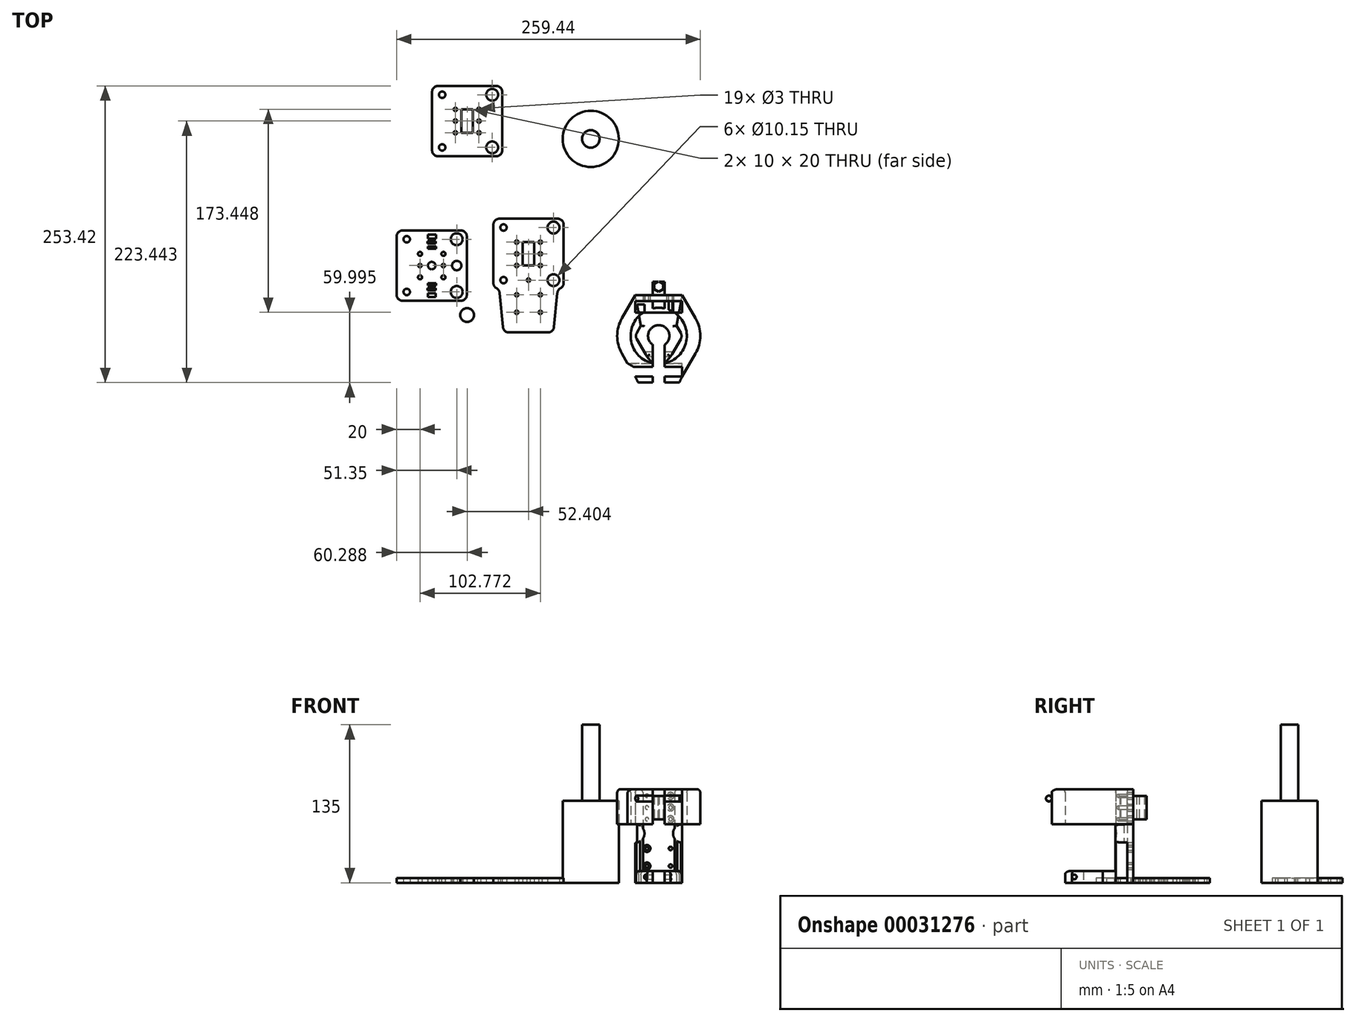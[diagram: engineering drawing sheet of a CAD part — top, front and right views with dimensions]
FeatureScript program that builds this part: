
annotation { "Feature Type Name" : "Feature", "Feature Type Description" : "" }
export const myFeature = defineFeature(function(context is Context, id is Id, definition is map)
    precondition{}
    {
        {
            var Q0;
            Q0=qCreatedBy(makeId("Top.planeOp"),FACE);
            var sketch = newSketch(context, id + "F0", { "sketchPlane" : qUnion([Q0])});
            skArc(sketch, "E0", {"start": v(24.79, -19.87) * mm, "mid": v(28.33, -18.4) * mm, "end": v(29.79, -14.87) * mm});
            skLineSegment(sketch, "E1", {"start": v(24.79, -19.87) * mm, "end": v(-25.21, -19.87) * mm});
            skArc(sketch, "E2", {"start": v(29.79, 35.13) * mm, "mid": v(28.33, 38.67) * mm, "end": v(24.79, 40.13) * mm});
            skLineSegment(sketch, "E3", {"start": v(29.79, 35.13) * mm, "end": v(29.79, -14.87) * mm});
            skArc(sketch, "E4", {"start": v(-25.21, 40.13) * mm, "mid": v(-28.75, 38.67) * mm, "end": v(-30.21, 35.13) * mm});
            skLineSegment(sketch, "E5", {"start": v(-25.21, 40.13) * mm, "end": v(24.79, 40.13) * mm});
            skArc(sketch, "E6", {"start": v(-30.21, -14.87) * mm, "mid": v(-28.75, -18.4) * mm, "end": v(-25.21, -19.87) * mm});
            skLineSegment(sketch, "E7", {"start": v(-30.21, -14.87) * mm, "end": v(-30.21, 35.13) * mm});
            skCircle(sketch, "E8", {"center": v(30, -32.16) * mm, "radius": 5.9 * mm});
            skCircle(sketch, "E9", {"center": v(-30, -32.16) * mm, "radius": 5.9 * mm});
            skLineSegment(sketch, "E10", {"start": v(-30.85, -40.13) * mm, "end": v(30.85, -40.13) * mm});
            skArc(sketch, "E11", {"start": v(30.85, -40.13) * mm, "mid": v(36.61, -37.74) * mm, "end": v(39, -31.98) * mm});
            skArc(sketch, "E12", {"start": v(39, -31.98) * mm, "mid": v(36.61, -26.22) * mm, "end": v(30.85, -23.83) * mm});
            skLineSegment(sketch, "E13", {"start": v(30.85, -23.83) * mm, "end": v(-30.85, -23.83) * mm});
            skArc(sketch, "E14", {"start": v(-30.85, -23.83) * mm, "mid": v(-36.61, -26.22) * mm, "end": v(-39, -31.98) * mm});
            skArc(sketch, "E15", {"start": v(-39, -31.98) * mm, "mid": v(-36.61, -37.74) * mm, "end": v(-30.85, -40.13) * mm});
            skCircle(sketch, "E16", {"center": v(21.14, 32.63) * mm, "radius": 5.08 * mm});
            skCircle(sketch, "E17", {"center": v(21.14, -12.37) * mm, "radius": 5.08 * mm});
            skCircle(sketch, "E18", {"center": v(-21.56, 32.63) * mm, "radius": 2.75 * mm});
            skCircle(sketch, "E19", {"center": v(-21.56, -12.37) * mm, "radius": 2.75 * mm});
            skCircle(sketch, "E20", {"center": v(-10.21, 20.13) * mm, "radius": 1.75 * mm});
            skCircle(sketch, "E21", {"center": v(-10.21, 0.13) * mm, "radius": 1.75 * mm});
            skCircle(sketch, "E22", {"center": v(9.79, 0.13) * mm, "radius": 1.75 * mm});
            skCircle(sketch, "E23", {"center": v(9.79, 20.13) * mm, "radius": 1.75 * mm});
            skLineSegment(sketch, "E24", {"start": v(-3.63, -6.88) * mm, "end": v(3.37, -6.88) * mm});
            skLineSegment(sketch, "E25", {"start": v(3.37, -6.88) * mm, "end": v(3.37, -4.88) * mm});
            skLineSegment(sketch, "E26", {"start": v(3.37, -4.88) * mm, "end": v(-3.63, -4.88) * mm});
            skLineSegment(sketch, "E27", {"start": v(-3.63, -4.88) * mm, "end": v(-3.63, -6.88) * mm});
            skLineSegment(sketch, "E28", {"start": v(-3.66, -11.08) * mm, "end": v(3.34, -11.08) * mm});
            skLineSegment(sketch, "E29", {"start": v(3.34, -11.08) * mm, "end": v(3.34, -9.08) * mm});
            skLineSegment(sketch, "E30", {"start": v(3.34, -9.08) * mm, "end": v(-3.66, -9.08) * mm});
            skLineSegment(sketch, "E31", {"start": v(-3.66, -9.08) * mm, "end": v(-3.66, -11.08) * mm});
            skLineSegment(sketch, "E32", {"start": v(3.35, -16.82) * mm, "end": v(3.35, -13.38) * mm});
            skLineSegment(sketch, "E33", {"start": v(3.35, -13.38) * mm, "end": v(-3.63, -13.38) * mm});
            skLineSegment(sketch, "E34", {"start": v(-3.63, 33.12) * mm, "end": v(3.37, 33.12) * mm});
            skLineSegment(sketch, "E35", {"start": v(3.37, 33.12) * mm, "end": v(3.37, 36.53) * mm});
            skLineSegment(sketch, "E36", {"start": v(3.37, 36.53) * mm, "end": v(-3.63, 36.52) * mm});
            skLineSegment(sketch, "E37", {"start": v(-3.63, 36.52) * mm, "end": v(-3.63, 33.12) * mm});
            skLineSegment(sketch, "E38", {"start": v(-3.66, 28.92) * mm, "end": v(3.34, 28.92) * mm});
            skLineSegment(sketch, "E39", {"start": v(3.34, 28.92) * mm, "end": v(3.34, 30.92) * mm});
            skLineSegment(sketch, "E40", {"start": v(3.34, 30.92) * mm, "end": v(-3.66, 30.92) * mm});
            skLineSegment(sketch, "E41", {"start": v(-3.66, 30.92) * mm, "end": v(-3.66, 28.92) * mm});
            skLineSegment(sketch, "E42", {"start": v(-3.63, 24.62) * mm, "end": v(3.37, 24.62) * mm});
            skLineSegment(sketch, "E43", {"start": v(3.37, 24.62) * mm, "end": v(3.37, 26.62) * mm});
            skLineSegment(sketch, "E44", {"start": v(3.37, 26.62) * mm, "end": v(-3.63, 26.62) * mm});
            skLineSegment(sketch, "E45", {"start": v(-3.63, 26.62) * mm, "end": v(-3.63, 24.62) * mm});
            skCircle(sketch, "E46", {"center": v(-10.21, 10.13) * mm, "radius": 1.5 * mm});
            skCircle(sketch, "E47", {"center": v(9.79, 10.13) * mm, "radius": 1.5 * mm});
            skCircle(sketch, "E48", {"center": v(-10.18, -31.98) * mm, "radius": 1.5 * mm});
            skCircle(sketch, "E49", {"center": v(9.82, -31.98) * mm, "radius": 1.5 * mm});
            skCircle(sketch, "E50", {"center": v(-0.21, 10.13) * mm, "radius": 3.2 * mm});
            skPoint(sketch, "E51", {"position": v(-3.63, 36.52) * mm});
            skLineSegment(sketch, "E52", {"start": v(-3.63, -16.82) * mm, "end": v(3.35, -16.82) * mm});
            skLineSegment(sketch, "E53", {"start": v(-3.63, -16.82) * mm, "end": v(-3.63, -13.38) * mm});
            skCircle(sketch, "E54", {"center": v(21.14, 10.13) * mm, "radius": 4 * mm});
            skLineSegment(sketch, "E55", {"start": v(112.48, 45.2) * mm, "end": v(112.48, -4.8) * mm});
            skLineSegment(sketch, "E56", {"start": v(57.48, 50.2) * mm, "end": v(107.48, 50.2) * mm});
            skLineSegment(sketch, "E57", {"start": v(52.48, -4.8) * mm, "end": v(52.48, 45.2) * mm});
            skCircle(sketch, "E58", {"center": v(103.83, 42.7) * mm, "radius": 5.08 * mm});
            skCircle(sketch, "E59", {"center": v(103.83, -2.3) * mm, "radius": 5.08 * mm});
            skCircle(sketch, "E60", {"center": v(61.13, -2.3) * mm, "radius": 2.75 * mm});
            skCircle(sketch, "E61", {"center": v(61.13, 42.7) * mm, "radius": 2.75 * mm});
            skArc(sketch, "E62", {"start": v(109.8, -9.23) * mm, "mid": v(111.76, -7.4) * mm, "end": v(112.48, -4.8) * mm});
            skArc(sketch, "E63", {"start": v(112.48, 45.2) * mm, "mid": v(111.02, 48.73) * mm, "end": v(107.48, 50.2) * mm});
            skArc(sketch, "E64", {"start": v(57.48, 50.2) * mm, "mid": v(53.95, 48.73) * mm, "end": v(52.48, 45.2) * mm});
            skArc(sketch, "E65", {"start": v(52.48, -4.8) * mm, "mid": v(53.95, -8.34) * mm, "end": v(57.48, -9.8) * mm});
            skLineSegment(sketch, "E66", {"start": v(82.48, -47) * mm, "end": v(82.48, -9.8) * mm, "construction": true});
            skLineSegment(sketch, "E67", {"start": v(82.48, -47) * mm, "end": v(99.3, -47) * mm});
            skLineSegment(sketch, "E68", {"start": v(107.15, -13.17) * mm, "end": v(104.27, -42.49) * mm});
            skPoint(sketch, "E69.visualSharp", {"position": v(107.48, -9.8) * mm});
            skArc(sketch, "E69.filletArc", {"start": v(109.8, -9.23) * mm, "mid": v(107.98, -10.87) * mm, "end": v(107.15, -13.17) * mm});
            skPoint(sketch, "E70.visualSharp", {"position": v(103.83, -47) * mm});
            skArc(sketch, "E70.filletArc", {"start": v(99.3, -47) * mm, "mid": v(102.66, -45.7) * mm, "end": v(104.27, -42.49) * mm});
            skLineSegment(sketch, "E71.MirrorCS", {"start": v(82.48, -47) * mm, "end": v(65.66, -47) * mm});
            skArc(sketch, "E72.MirrorCS", {"start": v(65.66, -47) * mm, "mid": v(62.3, -45.7) * mm, "end": v(60.69, -42.49) * mm});
            skLineSegment(sketch, "E73.MirrorCS", {"start": v(57.81, -13.17) * mm, "end": v(60.69, -42.49) * mm});
            skArc(sketch, "E74.MirrorCS", {"start": v(55.16, -9.23) * mm, "mid": v(56.98, -10.87) * mm, "end": v(57.81, -13.17) * mm});
            skLineSegment(sketch, "E75", {"start": v(82.48, 30.21) * mm, "end": v(87.48, 30.21) * mm});
            skLineSegment(sketch, "E76.bottom", {"start": v(87.48, 30.21) * mm, "end": v(77.48, 30.21) * mm});
            skLineSegment(sketch, "E76.left", {"start": v(87.48, 30.21) * mm, "end": v(87.48, 10.21) * mm});
            skLineSegment(sketch, "E76.right", {"start": v(77.48, 30.21) * mm, "end": v(77.48, 10.21) * mm});
            skLineSegment(sketch, "E77", {"start": v(92.56, 30.21) * mm, "end": v(92.56, 10.21) * mm, "construction": true});
            skLineSegment(sketch, "E78", {"start": v(87.48, 10.21) * mm, "end": v(77.48, 10.21) * mm});
            skCircle(sketch, "E79", {"center": v(92.56, 30.21) * mm, "radius": 1.5 * mm});
            skCircle(sketch, "E80", {"center": v(92.56, 20.21) * mm, "radius": 1.5 * mm});
            skCircle(sketch, "E81", {"center": v(92.56, 10.21) * mm, "radius": 1.5 * mm});
            skLineSegment(sketch, "E82", {"start": v(92.56, 10.21) * mm, "end": v(92.56, -14.79) * mm, "construction": true});
            skLineSegment(sketch, "E83", {"start": v(92.56, -14.79) * mm, "end": v(92.56, -29.79) * mm, "construction": true});
            skCircle(sketch, "E84", {"center": v(92.56, -14.79) * mm, "radius": 1.5 * mm});
            skCircle(sketch, "E85", {"center": v(92.56, -29.79) * mm, "radius": 1.5 * mm});
            skCircle(sketch, "E86.MirrorC", {"center": v(72.4, -14.79) * mm, "radius": 1.5 * mm});
            skCircle(sketch, "E87.MirrorC", {"center": v(72.4, -29.79) * mm, "radius": 1.5 * mm});
            skCircle(sketch, "E88.MirrorC", {"center": v(72.4, 10.21) * mm, "radius": 1.5 * mm});
            skCircle(sketch, "E89.MirrorC", {"center": v(72.4, 20.21) * mm, "radius": 1.5 * mm});
            skCircle(sketch, "E90.MirrorC", {"center": v(72.4, 30.21) * mm, "radius": 1.5 * mm});
            skLineSegment(sketch, "E91", {"start": v(60.08, 158.64) * mm, "end": v(60.08, 108.64) * mm});
            skLineSegment(sketch, "E92", {"start": v(5.08, 163.64) * mm, "end": v(55.08, 163.64) * mm});
            skLineSegment(sketch, "E93", {"start": v(0.08, 108.64) * mm, "end": v(0.08, 158.64) * mm});
            skCircle(sketch, "E94", {"center": v(51.43, 156.14) * mm, "radius": 5.08 * mm});
            skPoint(sketch, "E95.visualSharp", {"position": v(55.08, 103.64) * mm});
            skLineSegment(sketch, "E96.right", {"start": v(25.08, 143.66) * mm, "end": v(25.08, 123.66) * mm});
            skLineSegment(sketch, "E96.left", {"start": v(35.08, 143.66) * mm, "end": v(35.08, 123.66) * mm});
            skLineSegment(sketch, "E97", {"start": v(40.16, 143.66) * mm, "end": v(40.16, 123.66) * mm, "construction": true});
            skCircle(sketch, "E98", {"center": v(51.43, 111.14) * mm, "radius": 5.08 * mm});
            skCircle(sketch, "E99.MirrorC", {"center": v(20, 133.66) * mm, "radius": 1.5 * mm});
            skCircle(sketch, "E100", {"center": v(8.73, 111.14) * mm, "radius": 2.75 * mm});
            skCircle(sketch, "E101.MirrorC", {"center": v(20, 143.66) * mm, "radius": 1.5 * mm});
            skCircle(sketch, "E102", {"center": v(8.73, 156.14) * mm, "radius": 2.75 * mm});
            skCircle(sketch, "E103", {"center": v(40.16, 133.66) * mm, "radius": 1.5 * mm});
            skCircle(sketch, "E104.MirrorC", {"center": v(20, 123.66) * mm, "radius": 1.5 * mm});
            skLineSegment(sketch, "E96.bottom", {"start": v(35.08, 143.66) * mm, "end": v(25.08, 143.66) * mm});
            skArc(sketch, "E105", {"start": v(60.08, 158.64) * mm, "mid": v(58.61, 162.18) * mm, "end": v(55.08, 163.64) * mm});
            skLineSegment(sketch, "E106", {"start": v(35.08, 123.66) * mm, "end": v(25.08, 123.66) * mm});
            skArc(sketch, "E107", {"start": v(5.08, 163.64) * mm, "mid": v(1.54, 162.18) * mm, "end": v(0.08, 158.64) * mm});
            skCircle(sketch, "E108", {"center": v(40.16, 143.66) * mm, "radius": 1.5 * mm});
            skArc(sketch, "E109", {"start": v(0.08, 108.64) * mm, "mid": v(1.54, 105.1) * mm, "end": v(5.08, 103.64) * mm});
            skLineSegment(sketch, "E110", {"start": v(30.08, 143.66) * mm, "end": v(35.08, 143.66) * mm});
            skLineSegment(sketch, "E111", {"start": v(5.08, 103.64) * mm, "end": v(55.08, 103.64) * mm});
            skLineSegment(sketch, "E112", {"start": v(60.08, 108.64) * mm, "end": v(60.08, 108.64) * mm});
            skPoint(sketch, "E113.visualSharp", {"position": v(60.08, 103.64) * mm});
            skArc(sketch, "E113.filletArc", {"start": v(55.08, 103.64) * mm, "mid": v(58.61, 105.1) * mm, "end": v(60.08, 108.64) * mm});
            skCircle(sketch, "E114.MirrorC", {"center": v(40.16, 123.66) * mm, "radius": 1.5 * mm});
            skCircle(sketch, "E115", {"center": v(135.68, 118.4) * mm, "radius": 24 * mm});
            skCircle(sketch, "E116", {"center": v(135.68, 118.4) * mm, "radius": 7.5 * mm});
            skLineSegment(sketch, "E117", {"start": v(61.13, -2.3) * mm, "end": v(103.83, -2.3) * mm, "construction": true});
            skCircle(sketch, "E118", {"center": v(82.48, -2.3) * mm, "radius": 1.5 * mm});
            skArc(sketch, "E119.MirrorCS", {"start": v(112.48, -4.8) * mm, "mid": v(111.02, -8.34) * mm, "end": v(107.48, -9.8) * mm});
            skLineSegment(sketch, "E120", {"start": v(57.48, -9.8) * mm, "end": v(107.48, -9.8) * mm, "construction": true});
            skSolve(sketch);
        }
        {
            var Q0;
            Q0=makeQuery(id+"F0.imprint","IMPRINT",FACE,{"disambiguationData":[TD([[makeQuery(id+"F0.imprint","IMPRINT",EDGE,{"derivedFrom":sQuery(id+"F0.wireOp",EDGE,"E0")}),1.0]])]});
            var Q1;
            Q1=makeQuery(id+"F0.imprint","IMPRINT",FACE,{"disambiguationData":[TD([[makeQuery(id+"F0.imprint","IMPRINT",EDGE,{"derivedFrom":sQuery(id+"F0.wireOp",EDGE,"E8")}),1.0]])]});
            var Q2;
            Q2=makeQuery(id+"F0.imprint","IMPRINT",FACE,{"disambiguationData":[TD([[makeQuery(id+"F0.imprint","IMPRINT",EDGE,{"derivedFrom":sQuery(id+"F0.wireOp",EDGE,"f96d0108-ce3c-40f9-9041-a5f02a56c2c8")}),-1.0]])]});
            var Q3;
            Q3=makeQuery(id+"F0.imprint","IMPRINT",FACE,{"disambiguationData":[TD([[makeQuery(id+"F0.imprint","IMPRINT",EDGE,{"derivedFrom":sQuery(id+"F0.wireOp",EDGE,"fc6a74a1-8ae2-464b-8a54-e97a179053b1")}),1.0]])]});
            var Q4;
            Q4=makeQuery(id+"F0.imprint","IMPRINT",FACE,{"disambiguationData":[TD([[makeQuery(id+"F0.imprint","IMPRINT",EDGE,{"derivedFrom":sQuery(id+"F0.wireOp",EDGE,"E55")}),-1.0]])]});
            var Q5;
            Q5=makeQuery(id+"F0.imprint","IMPRINT",FACE,{"disambiguationData":[TD([[makeQuery(id+"F0.imprint","IMPRINT",EDGE,{"derivedFrom":sQuery(id+"F0.wireOp",EDGE,"E91")}),-1.0]])]});
            extrude(context, id + "F1", {"entities" : qUnion([Q0, Q1, Q2, Q3, Q4, Q5]), "depth" : 4 * mm});
        }
        {
            var Q0;
            Q0=qCreatedBy(makeId("Top.planeOp"),FACE);
            var sketch = newSketch(context, id + "F2", { "sketchPlane" : qUnion([Q0])});
            skCircle(sketch, "E121", {"center": v(193.74, -49.93) * mm, "radius": 9.15 * mm});
            skCircle(sketch, "E122.cCircle", {"center": v(193.74, -49.93) * mm, "radius": 17.57 * mm, "construction": true});
            skLineSegment(sketch, "E122.0", {"start": v(183.6, -32.36) * mm, "end": v(203.89, -32.36) * mm});
            skLineSegment(sketch, "E122.1", {"start": v(203.89, -32.36) * mm, "end": v(212.59, -47.43) * mm});
            skLineSegment(sketch, "E122.2", {"start": v(212.59, -52.43) * mm, "end": v(203.89, -67.5) * mm});
            skLineSegment(sketch, "E122.3", {"start": v(203.89, -67.5) * mm, "end": v(183.6, -67.5) * mm});
            skLineSegment(sketch, "E122.4", {"start": v(183.6, -67.5) * mm, "end": v(174.9, -52.43) * mm});
            skLineSegment(sketch, "E122.5", {"start": v(174.9, -47.43) * mm, "end": v(183.6, -32.36) * mm});
            skPoint(sketch, "E122.0.midPoint", {"position": v(193.74, -32.36) * mm});
            skCircle(sketch, "E123", {"center": v(193.74, -49.93) * mm, "radius": 24 * mm});
            skCircle(sketch, "E124.cCircle", {"center": v(193.74, -49.93) * mm, "radius": 34.75 * mm, "construction": true});
            skLineSegment(sketch, "E124.0", {"start": v(173.68, -15.18) * mm, "end": v(213.8, -15.18) * mm});
            skLineSegment(sketch, "E124.1", {"start": v(213.8, -15.18) * mm, "end": v(225.21, -34.93) * mm});
            skLineSegment(sketch, "E124.2", {"start": v(225.21, -64.93) * mm, "end": v(213.8, -84.68) * mm});
            skLineSegment(sketch, "E124.3", {"start": v(213.8, -84.68) * mm, "end": v(173.68, -84.68) * mm});
            skLineSegment(sketch, "E124.4", {"start": v(173.68, -84.68) * mm, "end": v(162.28, -64.93) * mm});
            skLineSegment(sketch, "E124.5", {"start": v(162.28, -34.93) * mm, "end": v(173.68, -15.18) * mm});
            skPoint(sketch, "E124.0.midPoint", {"position": v(193.74, -15.18) * mm});
            skLineSegment(sketch, "E125", {"start": v(193.74, -49.93) * mm, "end": v(193.74, -99) * mm, "construction": true});
            skPoint(sketch, "E125.endSnap0", {"position": v(193.74, -84.68) * mm});
            skLineSegment(sketch, "E126", {"start": v(193.74, -99) * mm, "end": v(198.74, -99) * mm, "construction": true});
            skLineSegment(sketch, "E127", {"start": v(198.74, -99) * mm, "end": v(198.74, -57.6) * mm});
            skLineSegment(sketch, "E128", {"start": v(198.74, -99) * mm, "end": v(206.95, -99) * mm});
            skLineSegment(sketch, "E129", {"start": v(206.95, -99) * mm, "end": v(213.8, -84.68) * mm});
            skLineSegment(sketch, "E130.MirrorCS", {"start": v(188.74, -99) * mm, "end": v(188.74, -57.6) * mm});
            skLineSegment(sketch, "E131.MirrorCS", {"start": v(188.74, -99) * mm, "end": v(180.54, -99) * mm});
            skLineSegment(sketch, "E132.MirrorCS", {"start": v(180.54, -99) * mm, "end": v(173.68, -84.68) * mm});
            skLineSegment(sketch, "E133", {"start": v(183.6, -67.5) * mm, "end": v(188.74, -73.4) * mm});
            skLineSegment(sketch, "E134.MirrorCS", {"start": v(203.89, -67.5) * mm, "end": v(198.74, -73.4) * mm, "construction": true});
            skLineSegment(sketch, "E135.MirrorCS", {"start": v(203.89, -67.5) * mm, "end": v(198.74, -73.4) * mm});
            skLineSegment(sketch, "E136", {"start": v(193.74, -49.93) * mm, "end": v(203.74, -49.93) * mm, "construction": true});
            skLineSegment(sketch, "E137", {"start": v(203.74, -49.93) * mm, "end": v(203.74, -15.18) * mm, "construction": true});
            skLineSegment(sketch, "E138.MirrorCS", {"start": v(183.74, -49.93) * mm, "end": v(183.74, -15.18) * mm, "construction": true});
            skLineSegment(sketch, "E139", {"start": v(178.53, -41.15) * mm, "end": v(173.68, -15.18) * mm});
            skLineSegment(sketch, "E140", {"start": v(208.96, -41.15) * mm, "end": v(213.8, -15.18) * mm});
            skPoint(sketch, "E141.visualSharp", {"position": v(153.62, -49.93) * mm});
            skArc(sketch, "E141.filletArc", {"start": v(162.28, -34.93) * mm, "mid": v(158.26, -49.93) * mm, "end": v(162.28, -64.93) * mm});
            skPoint(sketch, "E142.visualSharp", {"position": v(233.87, -49.93) * mm});
            skArc(sketch, "E142.filletArc", {"start": v(225.21, -64.93) * mm, "mid": v(229.23, -49.93) * mm, "end": v(225.21, -34.93) * mm});
            skPoint(sketch, "E143.visualSharp", {"position": v(173.46, -49.93) * mm});
            skArc(sketch, "E143.filletArc", {"start": v(174.9, -47.43) * mm, "mid": v(174.23, -49.93) * mm, "end": v(174.9, -52.43) * mm});
            skPoint(sketch, "E144.visualSharp", {"position": v(214.03, -49.93) * mm});
            skArc(sketch, "E144.filletArc", {"start": v(212.59, -52.43) * mm, "mid": v(213.26, -49.93) * mm, "end": v(212.59, -47.43) * mm});
            skCircle(sketch, "E145.cCircle", {"center": v(193.74, -7.9) * mm, "radius": 4.4 * mm, "construction": true});
            skLineSegment(sketch, "E145.0", {"start": v(193.74, -3.5) * mm, "end": v(197.55, -5.7) * mm});
            skLineSegment(sketch, "E145.1", {"start": v(197.55, -5.7) * mm, "end": v(197.55, -10.1) * mm});
            skLineSegment(sketch, "E145.2", {"start": v(197.55, -10.1) * mm, "end": v(193.74, -12.3) * mm});
            skLineSegment(sketch, "E145.3", {"start": v(193.74, -12.3) * mm, "end": v(189.94, -10.1) * mm});
            skLineSegment(sketch, "E145.4", {"start": v(189.94, -10.1) * mm, "end": v(189.94, -5.7) * mm});
            skLineSegment(sketch, "E145.5", {"start": v(189.94, -5.7) * mm, "end": v(193.74, -3.5) * mm});
            skCircle(sketch, "E146", {"center": v(193.74, -7.9) * mm, "radius": 2.5 * mm});
            skLineSegment(sketch, "E147", {"start": v(193.74, -15.18) * mm, "end": v(193.74, -11.18) * mm, "construction": true});
            skLineSegment(sketch, "E148", {"start": v(193.74, -11.18) * mm, "end": v(193.74, -7.9) * mm, "construction": true});
            skSolve(sketch);
        }
        {
            var Q0;
            {var subQ0=sQuery(id+"F2.wireOp",EDGE,"96ee02a5-edc4-4475-906e-b3a8b5a1a6cf");var subQ1=sQuery(id+"F2.wireOp",EDGE,"E123");var subQ2=makeQuery(id+"F2.imprint","INTERSECT",VERTEX,{"derivedFrom":[subQ1,subQ0]});Q0=makeQuery(id+"F2.imprint","IMPRINT",FACE,{"disambiguationData":[TD([[makeQuery(id+"F2.imprint","IMPRINT",EDGE,{"disambiguationData":[TD([[subQ2,1.0]])],"derivedFrom":subQ1}),-1.0]])]});}
            var Q1;
            {var subQ5=sQuery(id+"F2.wireOp",EDGE,"E124.0");Q1=makeQuery(id+"F2.imprint","IMPRINT",FACE,{"disambiguationData":[TD([[makeQuery(id+"F2.imprint","IMPRINT",EDGE,{"derivedFrom":subQ5}),-1.0]])]});}
            var Q2;
            {var subQ11=sQuery(id+"F2.wireOp",EDGE,"E122.0");Q2=makeQuery(id+"F2.imprint","IMPRINT",FACE,{"disambiguationData":[TD([[makeQuery(id+"F2.imprint","IMPRINT",EDGE,{"derivedFrom":subQ11}),-1.0]])]});}
            var Q3;
            {var subQ8=sQuery(id+"F2.wireOp",EDGE,"E122.0");Q3=makeQuery(id+"F2.imprint","IMPRINT",FACE,{"disambiguationData":[TD([[makeQuery(id+"F2.imprint","IMPRINT",EDGE,{"derivedFrom":subQ8}),1.0]])]});}
            var Q4;
            {var subQ0=sQuery(id+"F2.wireOp",EDGE,"E135.MirrorCS");Q4=makeQuery(id+"F2.imprint","IMPRINT",FACE,{"disambiguationData":[TD([[makeQuery(id+"F2.imprint","IMPRINT",EDGE,{"derivedFrom":subQ0}),-1.0]])]});}
            var Q5;
            {var subQ0=sQuery(id+"F2.wireOp",EDGE,"E133");Q5=makeQuery(id+"F2.imprint","IMPRINT",FACE,{"disambiguationData":[TD([[makeQuery(id+"F2.imprint","IMPRINT",EDGE,{"derivedFrom":subQ0}),1.0]])]});}
            extrude(context, id + "F3", {"entities" : qUnion([Q0, Q1, Q2, Q3, Q4, Q5]), "depth" : 10 * mm});
        }
        {
            var Q0;
            {var subQ5=sQuery(id+"F2.wireOp",EDGE,"E124.0");Q0=makeQuery(id+"F2.imprint","IMPRINT",FACE,{"disambiguationData":[TD([[makeQuery(id+"F2.imprint","IMPRINT",EDGE,{"derivedFrom":subQ5}),-1.0]])]});}
            extrude(context, id + "F4", {"entities" : qUnion([Q0]), "operationType" : NewBodyOperationType.ADD, "depth" : 80 * mm, "hasSecondDirection" : true, "secondDirectionOppositeDirection" : false, "secondDirectionDepth" : 10 * mm});
        }
        {
            var Q0;
            {var subQ1=sQuery(id+"F2.wireOp",EDGE,"E124.4");Q0=makeQuery(id+"F2.imprint","IMPRINT",FACE,{"disambiguationData":[TD([[makeQuery(id+"F2.imprint","IMPRINT",EDGE,{"derivedFrom":subQ1}),-1.0]])]});}
            var Q1;
            {var subQ4=sQuery(id+"F2.wireOp",EDGE,"E131.MirrorCS");Q1=makeQuery(id+"F2.imprint","IMPRINT",FACE,{"disambiguationData":[TD([[makeQuery(id+"F2.imprint","IMPRINT",EDGE,{"derivedFrom":subQ4}),-1.0]])]});}
            var Q2;
            {var subQ4=sQuery(id+"F2.wireOp",EDGE,"E128");Q2=makeQuery(id+"F2.imprint","IMPRINT",FACE,{"disambiguationData":[TD([[makeQuery(id+"F2.imprint","IMPRINT",EDGE,{"derivedFrom":subQ4}),1.0]])]});}
            var Q3;
            {var subQ6=sQuery(id+"F2.wireOp",EDGE,"E124.1");Q3=makeQuery(id+"F2.imprint","IMPRINT",FACE,{"disambiguationData":[TD([[makeQuery(id+"F2.imprint","IMPRINT",EDGE,{"derivedFrom":subQ6}),-1.0]])]});}
            var Q4;
            {var subQ5=sQuery(id+"F2.wireOp",EDGE,"E124.0");Q4=makeQuery(id+"F2.imprint","IMPRINT",FACE,{"disambiguationData":[TD([[makeQuery(id+"F2.imprint","IMPRINT",EDGE,{"derivedFrom":subQ5}),-1.0]])]});}
            extrude(context, id + "F5", {"entities" : qUnion([Q0, Q1, Q2, Q3, Q4]), "operationType" : NewBodyOperationType.ADD, "depth" : 80 * mm, "hasSecondDirection" : true, "secondDirectionOppositeDirection" : false, "secondDirectionDepth" : 50 * mm});
        }
        {
            var Q0;
            {var subQ0=sQuery(id+"F2.wireOp",EDGE,"E124.0");Q0=makeQuery(id+"F4.boolean.opBoolean","MERGE",FACE,{"derivedFrom":[makeQuery(id+"F3.opExtrude","SWEPT_FACE",FACE,{"disambiguationData":[OSD([subQ0])]}),makeQuery(id+"F4.opExtrude","SWEPT_FACE",FACE,{"disambiguationData":[OSD([subQ0])]})]});}
            var sketch = newSketch(context, id + "F6", { "sketchPlane" : qUnion([Q0])});
            skLineSegment(sketch, "E149", {"start": v(-193.74, 64.3) * mm, "end": v(-198.74, 64.3) * mm, "construction": true});
            skLineSegment(sketch, "E150", {"start": v(-198.74, 64.3) * mm, "end": v(-198.74, 54.3) * mm, "construction": true});
            skLineSegment(sketch, "E151", {"start": v(-198.74, 54.3) * mm, "end": v(-193.74, 54.3) * mm, "construction": true});
            skLineSegment(sketch, "E152.bottom", {"start": v(-198.74, 54.3) * mm, "end": v(-188.74, 54.3) * mm});
            skLineSegment(sketch, "E152.top", {"start": v(-198.74, 74.3) * mm, "end": v(-188.74, 74.3) * mm});
            skLineSegment(sketch, "E152.left", {"start": v(-198.74, 54.3) * mm, "end": v(-198.74, 74.3) * mm});
            skLineSegment(sketch, "E152.right", {"start": v(-188.74, 54.3) * mm, "end": v(-188.74, 74.3) * mm});
            skLineSegment(sketch, "E153", {"start": v(-188.74, 74.3) * mm, "end": v(-183.66, 74.3) * mm, "construction": true});
            skCircle(sketch, "E154", {"center": v(-183.66, 74.3) * mm, "radius": 1.5 * mm});
            skCircle(sketch, "E155", {"center": v(-183.66, 64.3) * mm, "radius": 1.5 * mm});
            skCircle(sketch, "E156", {"center": v(-183.66, 54.3) * mm, "radius": 1.5 * mm});
            skCircle(sketch, "E157", {"center": v(-173.68, 42.14) * mm, "radius": 7.86 * mm});
            skLineSegment(sketch, "E158", {"start": v(-193.74, 0) * mm, "end": v(-193.74, 29.82) * mm, "construction": true});
            skCircle(sketch, "E159.MirrorC", {"center": v(-213.8, 42.14) * mm, "radius": 7.86 * mm});
            skLineSegment(sketch, "E160", {"start": v(-193.74, 29.82) * mm, "end": v(-193.74, 54.3) * mm, "construction": true});
            skLineSegment(sketch, "E161", {"start": v(-203.82, 54.3) * mm, "end": v(-203.82, 29.3) * mm, "construction": true});
            skLineSegment(sketch, "E162", {"start": v(-203.82, 29.3) * mm, "end": v(-203.82, 14.3) * mm, "construction": true});
            skCircle(sketch, "E163", {"center": v(-203.82, 29.3) * mm, "radius": 1.5 * mm});
            skCircle(sketch, "E164", {"center": v(-203.82, 14.3) * mm, "radius": 1.5 * mm});
            skCircle(sketch, "E165.MirrorC", {"center": v(-183.66, 29.3) * mm, "radius": 1.5 * mm});
            skCircle(sketch, "E166.MirrorC", {"center": v(-183.66, 14.3) * mm, "radius": 1.5 * mm});
            skCircle(sketch, "E167", {"center": v(-183.66, 74.3) * mm, "radius": 3 * mm});
            skCircle(sketch, "E168", {"center": v(-183.66, 64.3) * mm, "radius": 3 * mm});
            skCircle(sketch, "E169", {"center": v(-183.66, 54.3) * mm, "radius": 3 * mm});
            skCircle(sketch, "E170", {"center": v(-183.66, 29.3) * mm, "radius": 3 * mm});
            skCircle(sketch, "E171", {"center": v(-183.66, 14.3) * mm, "radius": 3 * mm});
            skCircle(sketch, "E172.MirrorC", {"center": v(-203.82, 29.3) * mm, "radius": 3 * mm});
            skCircle(sketch, "E173.MirrorC", {"center": v(-203.82, 14.3) * mm, "radius": 3 * mm});
            skCircle(sketch, "E174.MirrorC", {"center": v(-203.82, 54.3) * mm, "radius": 3 * mm});
            skCircle(sketch, "E175.MirrorC", {"center": v(-203.82, 64.3) * mm, "radius": 3 * mm});
            skCircle(sketch, "E176.MirrorC", {"center": v(-203.82, 74.3) * mm, "radius": 3 * mm});
            skCircle(sketch, "E177.MirrorC", {"center": v(-203.82, 54.3) * mm, "radius": 1.5 * mm});
            skCircle(sketch, "E178.MirrorC", {"center": v(-203.82, 64.3) * mm, "radius": 1.5 * mm});
            skCircle(sketch, "E179.MirrorC", {"center": v(-203.82, 74.3) * mm, "radius": 1.5 * mm});
            skSolve(sketch);
        }
        {
            var Q0;
            Q0=makeQuery(id+"F6.imprint","IMPRINT",FACE,{"disambiguationData":[TD([[makeQuery(id+"F6.imprint","IMPRINT",EDGE,{"derivedFrom":sQuery(id+"F6.wireOp",EDGE,"E156")}),1.0]])]});
            var Q1;
            Q1=makeQuery(id+"F6.imprint","IMPRINT",FACE,{"disambiguationData":[TD([[makeQuery(id+"F6.imprint","IMPRINT",EDGE,{"derivedFrom":sQuery(id+"F6.wireOp",EDGE,"E155")}),1.0]])]});
            var Q2;
            Q2=makeQuery(id+"F6.imprint","IMPRINT",FACE,{"disambiguationData":[TD([[makeQuery(id+"F6.imprint","IMPRINT",EDGE,{"derivedFrom":sQuery(id+"F6.wireOp",EDGE,"E154")}),1.0]])]});
            var Q3;
            Q3=makeQuery(id+"F6.imprint","IMPRINT",FACE,{"disambiguationData":[TD([[makeQuery(id+"F6.imprint","IMPRINT",EDGE,{"derivedFrom":sQuery(id+"F6.wireOp",EDGE,"45766864-c449-461b-9b77-59a764d4195f0.MirrorC")}),-1.0]])]});
            var Q4;
            Q4=makeQuery(id+"F6.imprint","IMPRINT",FACE,{"disambiguationData":[TD([[makeQuery(id+"F6.imprint","IMPRINT",EDGE,{"derivedFrom":sQuery(id+"F6.wireOp",EDGE,"dd78de97-23d6-4229-883f-769f5d6694050.MirrorC")}),-1.0]])]});
            var Q5;
            Q5=makeQuery(id+"F6.imprint","IMPRINT",FACE,{"disambiguationData":[TD([[makeQuery(id+"F6.imprint","IMPRINT",EDGE,{"derivedFrom":sQuery(id+"F6.wireOp",EDGE,"2f0e754c-4723-4be7-9447-68277993e2870.MirrorC")}),-1.0]])]});
            var Q6;
            Q6=makeQuery(id+"F6.imprint","IMPRINT",FACE,{"disambiguationData":[TD([[makeQuery(id+"F6.imprint","IMPRINT",EDGE,{"derivedFrom":sQuery(id+"F6.wireOp",EDGE,"E177.MirrorC")}),-1.0]])]});
            var Q7;
            Q7=makeQuery(id+"F6.imprint","IMPRINT",FACE,{"disambiguationData":[TD([[makeQuery(id+"F6.imprint","IMPRINT",EDGE,{"derivedFrom":sQuery(id+"F6.wireOp",EDGE,"E178.MirrorC")}),-1.0]])]});
            var Q8;
            Q8=makeQuery(id+"F6.imprint","IMPRINT",FACE,{"disambiguationData":[TD([[makeQuery(id+"F6.imprint","IMPRINT",EDGE,{"derivedFrom":sQuery(id+"F6.wireOp",EDGE,"E179.MirrorC")}),-1.0]])]});
            var Q9;
            Q9=makeQuery(id+"F6.imprint","IMPRINT",FACE,{"disambiguationData":[TD([[makeQuery(id+"F6.imprint","IMPRINT",EDGE,{"derivedFrom":sQuery(id+"F6.wireOp",EDGE,"E163")}),1.0]])]});
            var Q10;
            Q10=makeQuery(id+"F6.imprint","IMPRINT",FACE,{"disambiguationData":[TD([[makeQuery(id+"F6.imprint","IMPRINT",EDGE,{"derivedFrom":sQuery(id+"F6.wireOp",EDGE,"E165.MirrorC")}),-1.0]])]});
            var Q11;
            Q11=makeQuery(id+"F6.imprint","IMPRINT",FACE,{"disambiguationData":[TD([[makeQuery(id+"F6.imprint","IMPRINT",EDGE,{"derivedFrom":sQuery(id+"F6.wireOp",EDGE,"E166.MirrorC")}),-1.0]])]});
            var Q12;
            Q12=makeQuery(id+"F6.imprint","IMPRINT",FACE,{"disambiguationData":[TD([[makeQuery(id+"F6.imprint","IMPRINT",EDGE,{"derivedFrom":sQuery(id+"F6.wireOp",EDGE,"E164")}),1.0]])]});
            extrude(context, id + "F7", {"entities" : qUnion([Q0, Q1, Q2, Q3, Q4, Q5, Q6, Q7, Q8, Q9, Q10, Q11, Q12]), "operationType" : NewBodyOperationType.REMOVE, "oppositeDirection" : true, "depth" : 25 * mm});
        }
        {
            var Q0;
            Q0=makeQuery(id+"F6.imprint","IMPRINT",FACE,{"disambiguationData":[TD([[makeQuery(id+"F6.imprint","IMPRINT",EDGE,{"derivedFrom":sQuery(id+"F6.wireOp",EDGE,"E152.bottom")}),1.0]])]});
            extrude(context, id + "F8", {"entities" : qUnion([Q0]), "operationType" : NewBodyOperationType.ADD, "depth" : 11.5 * mm});
        }
        {
            var Q0;
            {var subQ0=sQuery(id+"F6.wireOp",EDGE,"E159.MirrorC");var subQ1=sQuery(id+"F2.wireOp",EDGE,"E124.0");var subQ2=sQuery(id+"F2.wireOp",EDGE,"E140");var subQ3=sQuery(id+"F2.wireOp",EDGE,"E130.MirrorCS");var subQ4=sQuery(id+"F2.wireOp",EDGE,"E127");var subQ5=sQuery(id+"F2.wireOp",EDGE,"E124.1");var subQ6=makeQuery(id+"F4.boolean.opBoolean","MERGE",EDGE,{"derivedFrom":[makeQuery(id+"F3.opExtrude","SWEPT_EDGE",EDGE,{"disambiguationData":[OSD([subQ1,subQ5,subQ2])]}),makeQuery(id+"F4.opExtrude","SWEPT_EDGE",EDGE,{"disambiguationData":[OSD([subQ1,subQ5,subQ2])]})]});var subQ7=makeQuery(id+"F5.boolean.opBoolean","SPLIT",EDGE,{"disambiguationData":[TD([makeQuery(id+"F3.opExtrude","CAP_FACE",FACE,{"disambiguationData":[OSD([sQuery(id+"F2.wireOp",EDGE,"E121"),sQuery(id+"F2.wireOp",EDGE,"E122.1"),sQuery(id+"F2.wireOp",EDGE,"E122.2"),sQuery(id+"F2.wireOp",EDGE,"E122.4"),sQuery(id+"F2.wireOp",EDGE,"E122.5"),subQ1,subQ4,subQ3,sQuery(id+"F2.wireOp",EDGE,"E133"),sQuery(id+"F2.wireOp",EDGE,"E135.MirrorCS"),sQuery(id+"F2.wireOp",EDGE,"E139"),subQ2])],"isStart":true})])],"derivedFrom":subQ6});var subQ9=makeQuery(id+"F6.imprint","INTERSECT",VERTEX,{"derivedFrom":[subQ7,subQ0]});Q0=makeQuery(id+"F6.imprint","IMPRINT",FACE,{"disambiguationData":[TD([[makeQuery(id+"F6.imprint","IMPRINT",EDGE,{"disambiguationData":[TD([[subQ9,1.0]])],"derivedFrom":subQ0}),-1.0]])]});}
            var Q1;
            {var subQ0=sQuery(id+"F6.wireOp",EDGE,"E157");var subQ1=sQuery(id+"F2.wireOp",EDGE,"E124.0");var subQ2=sQuery(id+"F2.wireOp",EDGE,"E139");var subQ3=sQuery(id+"F2.wireOp",EDGE,"E130.MirrorCS");var subQ4=sQuery(id+"F2.wireOp",EDGE,"E127");var subQ5=sQuery(id+"F2.wireOp",EDGE,"E124.5");var subQ6=makeQuery(id+"F4.boolean.opBoolean","MERGE",EDGE,{"derivedFrom":[makeQuery(id+"F3.opExtrude","SWEPT_EDGE",EDGE,{"disambiguationData":[OSD([subQ1,subQ5,subQ2])]}),makeQuery(id+"F4.opExtrude","SWEPT_EDGE",EDGE,{"disambiguationData":[OSD([subQ1,subQ5,subQ2])]})]});var subQ7=makeQuery(id+"F5.boolean.opBoolean","SPLIT",EDGE,{"disambiguationData":[TD([makeQuery(id+"F3.opExtrude","CAP_FACE",FACE,{"disambiguationData":[OSD([sQuery(id+"F2.wireOp",EDGE,"E121"),sQuery(id+"F2.wireOp",EDGE,"E122.1"),sQuery(id+"F2.wireOp",EDGE,"E122.2"),sQuery(id+"F2.wireOp",EDGE,"E122.4"),sQuery(id+"F2.wireOp",EDGE,"E122.5"),subQ1,subQ4,subQ3,sQuery(id+"F2.wireOp",EDGE,"E133"),sQuery(id+"F2.wireOp",EDGE,"E135.MirrorCS"),subQ2,sQuery(id+"F2.wireOp",EDGE,"E140")])],"isStart":true})])],"derivedFrom":subQ6});var subQ9=makeQuery(id+"F6.imprint","INTERSECT",VERTEX,{"derivedFrom":[subQ7,subQ0]});Q1=makeQuery(id+"F6.imprint","IMPRINT",FACE,{"disambiguationData":[TD([[makeQuery(id+"F6.imprint","IMPRINT",EDGE,{"disambiguationData":[TD([[subQ9,1.0]])],"derivedFrom":subQ0}),1.0]])]});}
            extrude(context, id + "F9", {"entities" : qUnion([Q0, Q1]), "operationType" : NewBodyOperationType.REMOVE, "oppositeDirection" : true, "depth" : 8 * mm});
        }
        {
            var Q0;
            Q0=makeQuery(id+"F2.imprint","IMPRINT",FACE,{"disambiguationData":[TD([[makeQuery(id+"F2.imprint","IMPRINT",EDGE,{"derivedFrom":sQuery(id+"F2.wireOp",EDGE,"E146")}),1.0]])]});
            var Q1;
            Q1=makeQuery(id+"F2.imprint","IMPRINT",FACE,{"disambiguationData":[TD([[makeQuery(id+"F2.imprint","IMPRINT",EDGE,{"derivedFrom":sQuery(id+"F2.wireOp",EDGE,"E145.0")}),-1.0]])]});
            extrude(context, id + "F10", {"entities" : qUnion([Q0, Q1]), "operationType" : NewBodyOperationType.REMOVE, "depth" : 80 * mm});
        }
        {
            var Q0;
            Q0=makeQuery(id+"F5.opExtrude","CAP_EDGE",EDGE,{"disambiguationData":[OSD([sQuery(id+"F2.wireOp",EDGE,"E128")])],"isStart":false});
            var Q1;
            Q1=makeQuery(id+"F5.opExtrude","CAP_EDGE",EDGE,{"disambiguationData":[OSD([sQuery(id+"F2.wireOp",EDGE,"E129")])],"isStart":false});
            var Q2;
            Q2=makeQuery(id+"F5.opExtrude","CAP_EDGE",EDGE,{"disambiguationData":[OSD([sQuery(id+"F2.wireOp",EDGE,"E124.1")])],"isStart":false});
            var Q3;
            Q3=makeQuery(id+"F5.opExtrude","CAP_EDGE",EDGE,{"disambiguationData":[OSD([sQuery(id+"F2.wireOp",EDGE,"E124.5")])],"isStart":false});
            var Q4;
            Q4=makeQuery(id+"F5.opExtrude","CAP_EDGE",EDGE,{"disambiguationData":[OSD([sQuery(id+"F2.wireOp",EDGE,"E141.filletArc")])],"isStart":false});
            var Q5;
            Q5=makeQuery(id+"F4.opExtrude","CAP_EDGE",EDGE,{"disambiguationData":[OSD([sQuery(id+"F2.wireOp",EDGE,"E123")])],"isStart":false});
            var Q6;
            Q6=makeQuery(id+"F4.opExtrude","CAP_EDGE",EDGE,{"disambiguationData":[OSD([sQuery(id+"F2.wireOp",EDGE,"E139")])],"isStart":false});
            var Q7;
            Q7=makeQuery(id+"F4.opExtrude","CAP_EDGE",EDGE,{"disambiguationData":[OSD([sQuery(id+"F2.wireOp",EDGE,"E140")])],"isStart":false});
            var Q8;
            Q8=makeQuery(id+"F3.opExtrude","CAP_EDGE",EDGE,{"disambiguationData":[OSD([sQuery(id+"F2.wireOp",EDGE,"E140")])],"isStart":false});
            var Q9;
            Q9=makeQuery(id+"F3.opExtrude","CAP_EDGE",EDGE,{"disambiguationData":[OSD([sQuery(id+"F2.wireOp",EDGE,"E139")])],"isStart":false});
            var Q10;
            {var subQ0=sQuery(id+"F2.wireOp",EDGE,"E140");var subQ1=sQuery(id+"F2.wireOp",EDGE,"E123");var subQ2=sQuery(id+"F2.wireOp",EDGE,"E130.MirrorCS");var subQ3=sQuery(id+"F2.wireOp",EDGE,"E127");var subQ4=sQuery(id+"F2.wireOp",EDGE,"E124.0");Q10=makeQuery(id+"F5.boolean.opBoolean","SPLIT",EDGE,{"disambiguationData":[TD([makeQuery(id+"F3.opExtrude","CAP_FACE",FACE,{"disambiguationData":[OSD([sQuery(id+"F2.wireOp",EDGE,"E121"),sQuery(id+"F2.wireOp",EDGE,"E122.1"),sQuery(id+"F2.wireOp",EDGE,"E122.2"),sQuery(id+"F2.wireOp",EDGE,"E122.4"),sQuery(id+"F2.wireOp",EDGE,"E122.5"),subQ4,subQ3,subQ2,sQuery(id+"F2.wireOp",EDGE,"E133"),sQuery(id+"F2.wireOp",EDGE,"E135.MirrorCS"),sQuery(id+"F2.wireOp",EDGE,"E139"),subQ0,sQuery(id+"F2.wireOp",EDGE,"E143.filletArc"),sQuery(id+"F2.wireOp",EDGE,"E144.filletArc")])],"isStart":false})])],"derivedFrom":makeQuery(id+"F4.opExtrude","SWEPT_EDGE",EDGE,{"disambiguationData":[OSD([subQ1,subQ0])]})});}
            var Q11;
            {var subQ0=sQuery(id+"F2.wireOp",EDGE,"E140");var subQ1=sQuery(id+"F2.wireOp",EDGE,"E124.0");var subQ2=sQuery(id+"F2.wireOp",EDGE,"E123");Q11=makeQuery(id+"F5.boolean.opBoolean","SPLIT",EDGE,{"disambiguationData":[TD([makeQuery(id+"F4.opExtrude","CAP_FACE",FACE,{"disambiguationData":[OSD([subQ2,subQ1,sQuery(id+"F2.wireOp",EDGE,"E139"),subQ0])],"isStart":false})])],"derivedFrom":makeQuery(id+"F4.opExtrude","SWEPT_EDGE",EDGE,{"disambiguationData":[OSD([subQ2,subQ0])]})});}
            var Q12;
            Q12=makeQuery(id+"F3.opExtrude","CAP_EDGE",EDGE,{"disambiguationData":[OSD([sQuery(id+"F2.wireOp",EDGE,"E122.1")])],"isStart":false});
            var Q13;
            Q13=makeQuery(id+"F3.opExtrude","CAP_EDGE",EDGE,{"disambiguationData":[OSD([sQuery(id+"F2.wireOp",EDGE,"E122.2")])],"isStart":false});
            var Q14;
            Q14=makeQuery(id+"F3.opExtrude","CAP_EDGE",EDGE,{"disambiguationData":[OSD([sQuery(id+"F2.wireOp",EDGE,"E135.MirrorCS")])],"isStart":false});
            var Q15;
            Q15=makeQuery(id+"F3.opExtrude","CAP_EDGE",EDGE,{"disambiguationData":[OSD([sQuery(id+"F2.wireOp",EDGE,"E144.filletArc")])],"isStart":false});
            var Q16;
            Q16=makeQuery(id+"F3.opExtrude","CAP_EDGE",EDGE,{"disambiguationData":[OSD([sQuery(id+"F2.wireOp",EDGE,"E122.5")])],"isStart":false});
            var Q17;
            Q17=makeQuery(id+"F3.opExtrude","CAP_EDGE",EDGE,{"disambiguationData":[OSD([sQuery(id+"F2.wireOp",EDGE,"E143.filletArc")])],"isStart":false});
            var Q18;
            Q18=makeQuery(id+"F3.opExtrude","CAP_EDGE",EDGE,{"disambiguationData":[OSD([sQuery(id+"F2.wireOp",EDGE,"E122.4")])],"isStart":false});
            var Q19;
            Q19=makeQuery(id+"F3.opExtrude","CAP_EDGE",EDGE,{"disambiguationData":[OSD([sQuery(id+"F2.wireOp",EDGE,"E133")])],"isStart":false});
            var Q20;
            {var subQ0=sQuery(id+"F2.wireOp",EDGE,"E139");var subQ1=sQuery(id+"F2.wireOp",EDGE,"E124.0");var subQ2=sQuery(id+"F2.wireOp",EDGE,"E123");Q20=makeQuery(id+"F5.boolean.opBoolean","SPLIT",EDGE,{"disambiguationData":[TD([makeQuery(id+"F4.opExtrude","CAP_FACE",FACE,{"disambiguationData":[OSD([subQ2,subQ1,subQ0,sQuery(id+"F2.wireOp",EDGE,"E140")])],"isStart":false})])],"derivedFrom":makeQuery(id+"F4.opExtrude","SWEPT_EDGE",EDGE,{"disambiguationData":[OSD([subQ2,subQ0])]})});}
            var Q21;
            {var subQ0=sQuery(id+"F2.wireOp",EDGE,"E139");var subQ1=sQuery(id+"F2.wireOp",EDGE,"E123");var subQ2=sQuery(id+"F2.wireOp",EDGE,"E130.MirrorCS");var subQ3=sQuery(id+"F2.wireOp",EDGE,"E127");var subQ4=sQuery(id+"F2.wireOp",EDGE,"E124.0");Q21=makeQuery(id+"F5.boolean.opBoolean","SPLIT",EDGE,{"disambiguationData":[TD([makeQuery(id+"F3.opExtrude","CAP_FACE",FACE,{"disambiguationData":[OSD([sQuery(id+"F2.wireOp",EDGE,"E121"),sQuery(id+"F2.wireOp",EDGE,"E122.1"),sQuery(id+"F2.wireOp",EDGE,"E122.2"),sQuery(id+"F2.wireOp",EDGE,"E122.4"),sQuery(id+"F2.wireOp",EDGE,"E122.5"),subQ4,subQ3,subQ2,sQuery(id+"F2.wireOp",EDGE,"E133"),sQuery(id+"F2.wireOp",EDGE,"E135.MirrorCS"),subQ0,sQuery(id+"F2.wireOp",EDGE,"E140"),sQuery(id+"F2.wireOp",EDGE,"E143.filletArc"),sQuery(id+"F2.wireOp",EDGE,"E144.filletArc")])],"isStart":false})])],"derivedFrom":makeQuery(id+"F4.opExtrude","SWEPT_EDGE",EDGE,{"disambiguationData":[OSD([subQ1,subQ0])]})});}
            var Q22;
            Q22=makeQuery(id+"F5.opExtrude","CAP_EDGE",EDGE,{"disambiguationData":[OSD([sQuery(id+"F2.wireOp",EDGE,"E131.MirrorCS")])],"isStart":false});
            fillet(context, id + "F11", {"entities" : qUnion([Q0, Q1, Q2, Q3, Q4, Q5, Q6, Q7, Q8, Q9, Q10, Q11, Q12, Q13, Q14, Q15, Q16, Q17, Q18, Q19, Q20, Q21, Q22]), "radius" : 3 * mm, "tangentPropagation" : true, "allowEdgeOverflow" : false});
        }
        {
            var Q0;
            Q0=makeQuery(id+"F3.opExtrude","SWEPT_FACE",FACE,{"disambiguationData":[OSD([sQuery(id+"F2.wireOp",EDGE,"E130.MirrorCS")])]});
            var sketch = newSketch(context, id + "F12", { "sketchPlane" : qUnion([Q0])});
            skLineSegment(sketch, "E180", {"start": v(-73.4, 0) * mm, "end": v(-57.6, 10) * mm, "construction": true});
            skCircle(sketch, "E181", {"center": v(-65.5, 5) * mm, "radius": 2 * mm});
            skSolve(sketch);
        }
        {
            var Q0;
            Q0=makeQuery(id+"F12.imprint","IMPRINT",FACE,{"disambiguationData":[TD([[makeQuery(id+"F12.imprint","IMPRINT",EDGE,{"derivedFrom":sQuery(id+"F12.wireOp",EDGE,"E181")}),1.0]])]});
            extrude(context, id + "F13", {"entities" : qUnion([Q0]), "operationType" : NewBodyOperationType.REMOVE, "oppositeDirection" : true, "depth" : 25 * mm, "hasSecondDirection" : true, "secondDirectionOppositeDirection" : false, "secondDirectionDepth" : 25 * mm});
        }
        {
            var Q0;
            Q0=makeQuery(id+"F5.opExtrude","SWEPT_FACE",FACE,{"disambiguationData":[OSD([sQuery(id+"F2.wireOp",EDGE,"E130.MirrorCS")])]});
            var sketch = newSketch(context, id + "F14", { "sketchPlane" : qUnion([Q0])});
            skLineSegment(sketch, "E182", {"start": v(-99, 50) * mm, "end": v(-75.55, 60) * mm, "construction": true});
            skCircle(sketch, "E183", {"center": v(-87.28, 55) * mm, "radius": 2.5 * mm});
            skLineSegment(sketch, "E184", {"start": v(-99, 63.5) * mm, "end": v(-87.5, 63.5) * mm, "construction": true});
            skCircle(sketch, "E185.MirrorC", {"center": v(-87.28, 72) * mm, "radius": 2.5 * mm});
            skSolve(sketch);
        }
        {
            var Q0;
            Q0=makeQuery(id+"F14.imprint","IMPRINT",FACE,{"disambiguationData":[TD([[makeQuery(id+"F14.imprint","IMPRINT",EDGE,{"derivedFrom":sQuery(id+"F14.wireOp",EDGE,"E183")}),1.0]])]});
            var Q1;
            Q1=makeQuery(id+"F14.imprint","IMPRINT",FACE,{"disambiguationData":[TD([[makeQuery(id+"F14.imprint","IMPRINT",EDGE,{"derivedFrom":sQuery(id+"F14.wireOp",EDGE,"E185.MirrorC")}),-1.0]])]});
            var Q2;
            Q2=sQuery(id+"F14.wireOp",EDGE,"E183");
            extrude(context, id + "F15", {"entities" : qUnion([Q0, Q1]), "operationType" : NewBodyOperationType.REMOVE, "surfaceEntities" : qUnion([Q2]), "oppositeDirection" : true, "depth" : 25 * mm, "hasSecondDirection" : true, "secondDirectionOppositeDirection" : false, "secondDirectionDepth" : 25 * mm});
        }
        {
            var Q0;
            Q0=makeQuery(id+"F6.imprint","IMPRINT",FACE,{"disambiguationData":[TD([[makeQuery(id+"F6.imprint","IMPRINT",EDGE,{"derivedFrom":sQuery(id+"F6.wireOp",EDGE,"E176.MirrorC")}),-1.0]])]});
            var Q1;
            Q1=makeQuery(id+"F6.imprint","IMPRINT",FACE,{"disambiguationData":[TD([[makeQuery(id+"F6.imprint","IMPRINT",EDGE,{"derivedFrom":sQuery(id+"F6.wireOp",EDGE,"E154")}),-1.0]])]});
            var Q2;
            Q2=makeQuery(id+"F6.imprint","IMPRINT",FACE,{"disambiguationData":[TD([[makeQuery(id+"F6.imprint","IMPRINT",EDGE,{"derivedFrom":sQuery(id+"F6.wireOp",EDGE,"E155")}),-1.0]])]});
            var Q3;
            Q3=makeQuery(id+"F6.imprint","IMPRINT",FACE,{"disambiguationData":[TD([[makeQuery(id+"F6.imprint","IMPRINT",EDGE,{"derivedFrom":sQuery(id+"F6.wireOp",EDGE,"E156")}),-1.0]])]});
            var Q4;
            Q4=makeQuery(id+"F6.imprint","IMPRINT",FACE,{"disambiguationData":[TD([[makeQuery(id+"F6.imprint","IMPRINT",EDGE,{"derivedFrom":sQuery(id+"F6.wireOp",EDGE,"E175.MirrorC")}),-1.0]])]});
            var Q5;
            Q5=makeQuery(id+"F6.imprint","IMPRINT",FACE,{"disambiguationData":[TD([[makeQuery(id+"F6.imprint","IMPRINT",EDGE,{"derivedFrom":sQuery(id+"F6.wireOp",EDGE,"E174.MirrorC")}),-1.0]])]});
            var Q6;
            Q6=makeQuery(id+"F6.imprint","IMPRINT",FACE,{"disambiguationData":[TD([[makeQuery(id+"F6.imprint","IMPRINT",EDGE,{"derivedFrom":sQuery(id+"F6.wireOp",EDGE,"E163")}),-1.0]])]});
            var Q7;
            Q7=makeQuery(id+"F6.imprint","IMPRINT",FACE,{"disambiguationData":[TD([[makeQuery(id+"F6.imprint","IMPRINT",EDGE,{"derivedFrom":sQuery(id+"F6.wireOp",EDGE,"E165.MirrorC")}),1.0]])]});
            var Q8;
            Q8=makeQuery(id+"F6.imprint","IMPRINT",FACE,{"disambiguationData":[TD([[makeQuery(id+"F6.imprint","IMPRINT",EDGE,{"derivedFrom":sQuery(id+"F6.wireOp",EDGE,"E166.MirrorC")}),1.0]])]});
            var Q9;
            Q9=makeQuery(id+"F6.imprint","IMPRINT",FACE,{"disambiguationData":[TD([[makeQuery(id+"F6.imprint","IMPRINT",EDGE,{"derivedFrom":sQuery(id+"F6.wireOp",EDGE,"E164")}),-1.0]])]});
            extrude(context, id + "F16", {"entities" : qUnion([Q0, Q1, Q2, Q3, Q4, Q5, Q6, Q7, Q8, Q9]), "operationType" : NewBodyOperationType.REMOVE, "oppositeDirection" : true, "depth" : 14.88 * mm, "hasSecondDirection" : true, "secondDirectionOppositeDirection" : true, "secondDirectionDepth" : 5 * mm});
        }
        {
            var Q0;
            Q0=makeQuery(id+"F0.imprint","IMPRINT",FACE,{"disambiguationData":[TD([[makeQuery(id+"F0.imprint","IMPRINT",EDGE,{"derivedFrom":sQuery(id+"F0.wireOp",EDGE,"E115")}),1.0]])]});
            extrude(context, id + "F17", {"entities" : qUnion([Q0]), "depth" : 70 * mm});
        }
        {
            var Q0;
            Q0=makeQuery(id+"F0.imprint","IMPRINT",FACE,{"disambiguationData":[TD([[makeQuery(id+"F0.imprint","IMPRINT",EDGE,{"derivedFrom":sQuery(id+"F0.wireOp",EDGE,"E116")}),1.0]])]});
            extrude(context, id + "F18", {"entities" : qUnion([Q0]), "operationType" : NewBodyOperationType.ADD, "depth" : 135 * mm});
        }
    });
